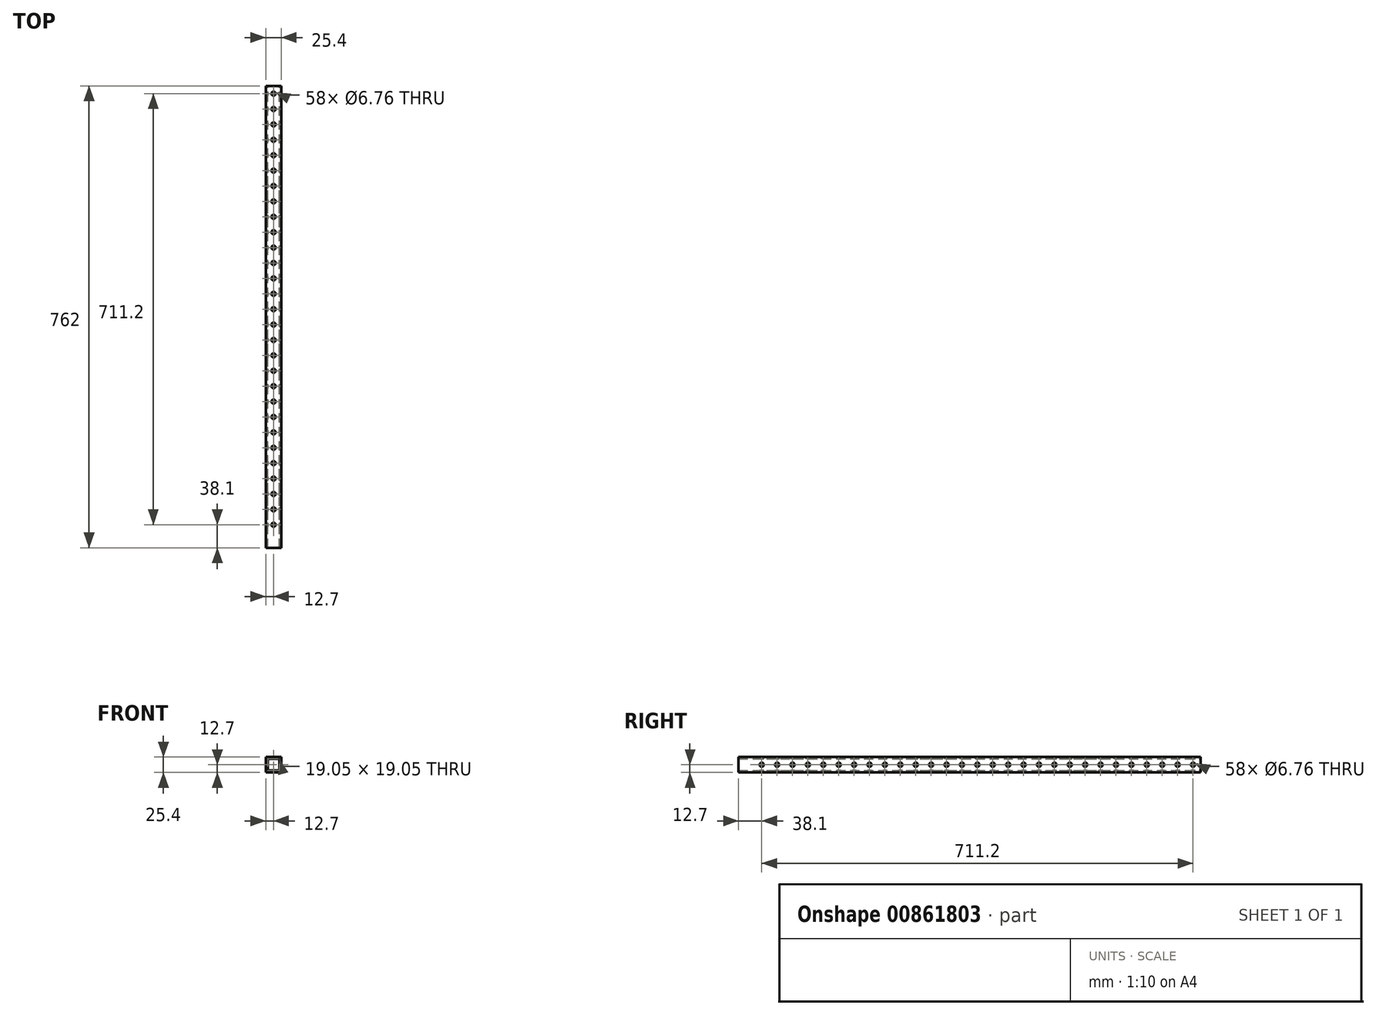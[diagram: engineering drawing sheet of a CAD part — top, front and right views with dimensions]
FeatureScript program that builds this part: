
annotation { "Feature Type Name" : "Feature", "Feature Type Description" : "" }
export const myFeature = defineFeature(function(context is Context, id is Id, definition is map)
    precondition{}
    {
        {
            var Q0;
            Q0=qCreatedBy(makeId("Front.planeOp"),FACE);
            var sketch = newSketch(context, id + "F0", { "sketchPlane" : qUnion([Q0])});
            skLineSegment(sketch, "E0.bottom", {"start": v(12.7, 12.7) * mm, "end": v(-12.7, 12.7) * mm});
            skLineSegment(sketch, "E0.top", {"start": v(12.7, -12.7) * mm, "end": v(-12.7, -12.7) * mm});
            skLineSegment(sketch, "E0.left", {"start": v(12.7, 12.7) * mm, "end": v(12.7, -12.7) * mm});
            skLineSegment(sketch, "E0.right", {"start": v(-12.7, 12.7) * mm, "end": v(-12.7, -12.7) * mm});
            skPoint(sketch, "E0.middle", {"position": v(0, 0) * mm});
            skLineSegment(sketch, "E1.bottom", {"start": v(9.53, -9.52) * mm, "end": v(-9.52, -9.53) * mm});
            skLineSegment(sketch, "E1.top", {"start": v(9.52, 9.53) * mm, "end": v(-9.53, 9.53) * mm});
            skLineSegment(sketch, "E1.left", {"start": v(9.52, 9.53) * mm, "end": v(9.53, -9.52) * mm});
            skLineSegment(sketch, "E1.right", {"start": v(-9.53, 9.53) * mm, "end": v(-9.52, -9.53) * mm});
            skSolve(sketch);
        }
        {
            var Q0;
            Q0=makeQuery(id+"F0.imprint","IMPRINT",FACE,{"disambiguationData":[TD([[makeQuery(id+"F0.imprint","IMPRINT",EDGE,{"derivedFrom":sQuery(id+"F0.wireOp",EDGE,"E0.bottom")}),1.0]])]});
            extrude(context, id + "F1", {"entities" : qUnion([Q0]), "depth" : 762 * mm, "offsetDistance" : 25.4 * mm, "symmetric" : true});
        }
        {
            var Q0;
            Q0=makeQuery(id+"F1.opExtrude","SWEPT_FACE",FACE,{"disambiguationData":[OSD([sQuery(id+"F0.wireOp",EDGE,"E0.bottom")])]});
            var sketch = newSketch(context, id + "F2", { "sketchPlane" : qUnion([Q0])});
            skCircle(sketch, "E2", {"center": v(0, -342.9) * mm, "radius": 3.38 * mm});
            skCircle(sketch, "E3.0.1.0", {"center": v(0, -317.5) * mm, "radius": 3.38 * mm});
            skCircle(sketch, "E3.0.2.0", {"center": v(0, -292.1) * mm, "radius": 3.38 * mm});
            skCircle(sketch, "E3.0.3.0", {"center": v(0, -266.7) * mm, "radius": 3.38 * mm});
            skCircle(sketch, "E3.0.4.0", {"center": v(0, -241.3) * mm, "radius": 3.38 * mm});
            skCircle(sketch, "E3.0.5.0", {"center": v(0, -215.9) * mm, "radius": 3.38 * mm});
            skCircle(sketch, "E3.0.6.0", {"center": v(0, -190.5) * mm, "radius": 3.38 * mm});
            skCircle(sketch, "E3.0.7.0", {"center": v(0, -165.1) * mm, "radius": 3.38 * mm});
            skCircle(sketch, "E3.0.8.0", {"center": v(0, -139.7) * mm, "radius": 3.38 * mm});
            skCircle(sketch, "E3.0.9.0", {"center": v(0, -114.3) * mm, "radius": 3.38 * mm});
            skCircle(sketch, "E3.0.10.0", {"center": v(0, -88.9) * mm, "radius": 3.38 * mm});
            skCircle(sketch, "E3.0.11.0", {"center": v(0, -63.5) * mm, "radius": 3.38 * mm});
            skCircle(sketch, "E3.0.12.0", {"center": v(0, -38.1) * mm, "radius": 3.38 * mm});
            skCircle(sketch, "E3.0.13.0", {"center": v(0, -12.7) * mm, "radius": 3.38 * mm});
            skCircle(sketch, "E3.0.14.0", {"center": v(0, 12.7) * mm, "radius": 3.38 * mm});
            skCircle(sketch, "E3.0.15.0", {"center": v(0, 38.1) * mm, "radius": 3.38 * mm});
            skCircle(sketch, "E3.0.16.0", {"center": v(0, 63.5) * mm, "radius": 3.38 * mm});
            skCircle(sketch, "E3.0.17.0", {"center": v(0, 88.9) * mm, "radius": 3.38 * mm});
            skCircle(sketch, "E3.0.18.0", {"center": v(0, 114.3) * mm, "radius": 3.38 * mm});
            skCircle(sketch, "E3.0.19.0", {"center": v(0, 139.7) * mm, "radius": 3.38 * mm});
            skCircle(sketch, "E3.0.20.0", {"center": v(0, 165.1) * mm, "radius": 3.38 * mm});
            skCircle(sketch, "E3.0.21.0", {"center": v(0, 190.5) * mm, "radius": 3.38 * mm});
            skCircle(sketch, "E3.0.22.0", {"center": v(0, 215.9) * mm, "radius": 3.38 * mm});
            skCircle(sketch, "E3.0.23.0", {"center": v(0, 241.3) * mm, "radius": 3.38 * mm});
            skCircle(sketch, "E3.0.24.0", {"center": v(0, 266.7) * mm, "radius": 3.38 * mm});
            skCircle(sketch, "E3.0.25.0", {"center": v(0, 292.1) * mm, "radius": 3.38 * mm});
            skCircle(sketch, "E3.0.26.0", {"center": v(0, 317.5) * mm, "radius": 3.38 * mm});
            skCircle(sketch, "E3.0.27.0", {"center": v(0, 342.9) * mm, "radius": 3.38 * mm});
            skLineSegment(sketch, "E3.direction1", {"start": v(0, -342.9) * mm, "end": v(25.4, -342.9) * mm, "construction": true});
            skLineSegment(sketch, "E3.direction2", {"start": v(0, -342.9) * mm, "end": v(0, -317.5) * mm, "construction": true});
            skCircle(sketch, "E4.0.0.28", {"center": v(0, 368.3) * mm, "radius": 3.38 * mm});
            skCircle(sketch, "E4.0.0.29", {"center": v(0, 393.7) * mm, "radius": 3.38 * mm});
            skSolve(sketch);
        }
        {
            var Q0;
            Q0 = qSketchRegion(id + "F2", true);
            var Q1;
            Q1=makeQuery(id+"F1.opExtrude","SWEPT_FACE",FACE,{"disambiguationData":[OSD([sQuery(id+"F0.wireOp",EDGE,"E0.top")])]});
            extrude(context, id + "F3", {"entities" : qUnion([Q0]), "operationType" : NewBodyOperationType.REMOVE, "endBound" : BoundingType.UP_TO_SURFACE, "oppositeDirection" : true, "depth" : 25.4 * mm, "endBoundEntityFace" : qUnion([Q1]), "offsetDistance" : 25.4 * mm});
        }
        {
            var Q0;
            Q0=makeQuery(id+"F1.opExtrude","SWEPT_FACE",FACE,{"disambiguationData":[OSD([sQuery(id+"F0.wireOp",EDGE,"E0.left")])]});
            var sketch = newSketch(context, id + "F4", { "sketchPlane" : qUnion([Q0])});
            skCircle(sketch, "E5", {"center": v(-342.9, 0) * mm, "radius": 3.38 * mm});
            skCircle(sketch, "E6.0.1.0", {"center": v(-317.5, 0) * mm, "radius": 3.38 * mm});
            skCircle(sketch, "E6.0.2.0", {"center": v(-292.1, 0) * mm, "radius": 3.38 * mm});
            skCircle(sketch, "E6.0.3.0", {"center": v(-266.7, 0) * mm, "radius": 3.38 * mm});
            skCircle(sketch, "E6.0.4.0", {"center": v(-241.3, 0) * mm, "radius": 3.38 * mm});
            skCircle(sketch, "E6.0.5.0", {"center": v(-215.9, 0) * mm, "radius": 3.38 * mm});
            skCircle(sketch, "E6.0.6.0", {"center": v(-190.5, 0) * mm, "radius": 3.38 * mm});
            skCircle(sketch, "E6.0.7.0", {"center": v(-165.1, 0) * mm, "radius": 3.38 * mm});
            skCircle(sketch, "E6.0.8.0", {"center": v(-139.7, 0) * mm, "radius": 3.38 * mm});
            skCircle(sketch, "E6.0.9.0", {"center": v(-114.3, 0) * mm, "radius": 3.38 * mm});
            skCircle(sketch, "E6.0.10.0", {"center": v(-88.9, 0) * mm, "radius": 3.38 * mm});
            skCircle(sketch, "E6.0.11.0", {"center": v(-63.5, 0) * mm, "radius": 3.38 * mm});
            skCircle(sketch, "E6.0.12.0", {"center": v(-38.1, 0) * mm, "radius": 3.38 * mm});
            skCircle(sketch, "E6.0.13.0", {"center": v(-12.7, 0) * mm, "radius": 3.38 * mm});
            skCircle(sketch, "E6.0.14.0", {"center": v(12.7, 0) * mm, "radius": 3.38 * mm});
            skCircle(sketch, "E6.0.15.0", {"center": v(38.1, 0) * mm, "radius": 3.38 * mm});
            skCircle(sketch, "E6.0.16.0", {"center": v(63.5, 0) * mm, "radius": 3.38 * mm});
            skCircle(sketch, "E6.0.17.0", {"center": v(88.9, 0) * mm, "radius": 3.38 * mm});
            skCircle(sketch, "E6.0.18.0", {"center": v(114.3, 0) * mm, "radius": 3.38 * mm});
            skCircle(sketch, "E6.0.19.0", {"center": v(139.7, 0) * mm, "radius": 3.38 * mm});
            skCircle(sketch, "E6.0.20.0", {"center": v(165.1, 0) * mm, "radius": 3.38 * mm});
            skCircle(sketch, "E6.0.21.0", {"center": v(190.5, 0) * mm, "radius": 3.38 * mm});
            skCircle(sketch, "E6.0.22.0", {"center": v(215.9, 0) * mm, "radius": 3.38 * mm});
            skCircle(sketch, "E6.0.23.0", {"center": v(241.3, 0) * mm, "radius": 3.38 * mm});
            skCircle(sketch, "E6.0.24.0", {"center": v(266.7, 0) * mm, "radius": 3.38 * mm});
            skCircle(sketch, "E6.0.25.0", {"center": v(292.1, 0) * mm, "radius": 3.38 * mm});
            skCircle(sketch, "E6.0.26.0", {"center": v(317.5, 0) * mm, "radius": 3.38 * mm});
            skCircle(sketch, "E6.0.27.0", {"center": v(342.9, 0) * mm, "radius": 3.38 * mm});
            skLineSegment(sketch, "E6.direction1", {"start": v(-342.9, 0) * mm, "end": v(-342.9, -26.56) * mm, "construction": true});
            skLineSegment(sketch, "E6.direction2", {"start": v(-342.9, 0) * mm, "end": v(-317.5, 0) * mm, "construction": true});
            skCircle(sketch, "E7.0.0.28", {"center": v(368.3, 0) * mm, "radius": 3.38 * mm});
            skCircle(sketch, "E7.0.0.29", {"center": v(393.7, 0) * mm, "radius": 3.38 * mm});
            skSolve(sketch);
        }
        {
            var Q0;
            Q0 = qSketchRegion(id + "F4", true);
            extrude(context, id + "F5", {"entities" : qUnion([Q0]), "operationType" : NewBodyOperationType.REMOVE, "oppositeDirection" : true, "depth" : 25.4 * mm, "offsetDistance" : 25.4 * mm});
        }
    });
